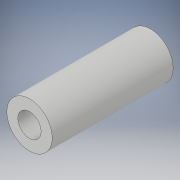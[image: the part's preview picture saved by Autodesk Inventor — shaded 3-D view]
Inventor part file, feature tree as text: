
AUTODESK INVENTOR PART (.ipt)
format: ipt  version: 2018 (Build 220112000, 112)  size: 95,232 bytes
history: native  units: in
note: dims shown in document units (in); Inventor stores cm internally (conversion verified against a paired STEP export)
features: extrude x1, sketch x1
ambient origin geometry x8: Origin, YZ Plane, XZ Plane, XY Plane, X Axis, Y Axis, Z Axis, Center Point
bodies: Solid1 (feature_tree)
feature tree (2):
  extrude  "Extrusion1"  Depth=1.0in
  sketch  "Sketch1"  dims[d0=0.375in d1=0.192in d2=1.0in d3=0.0in]
